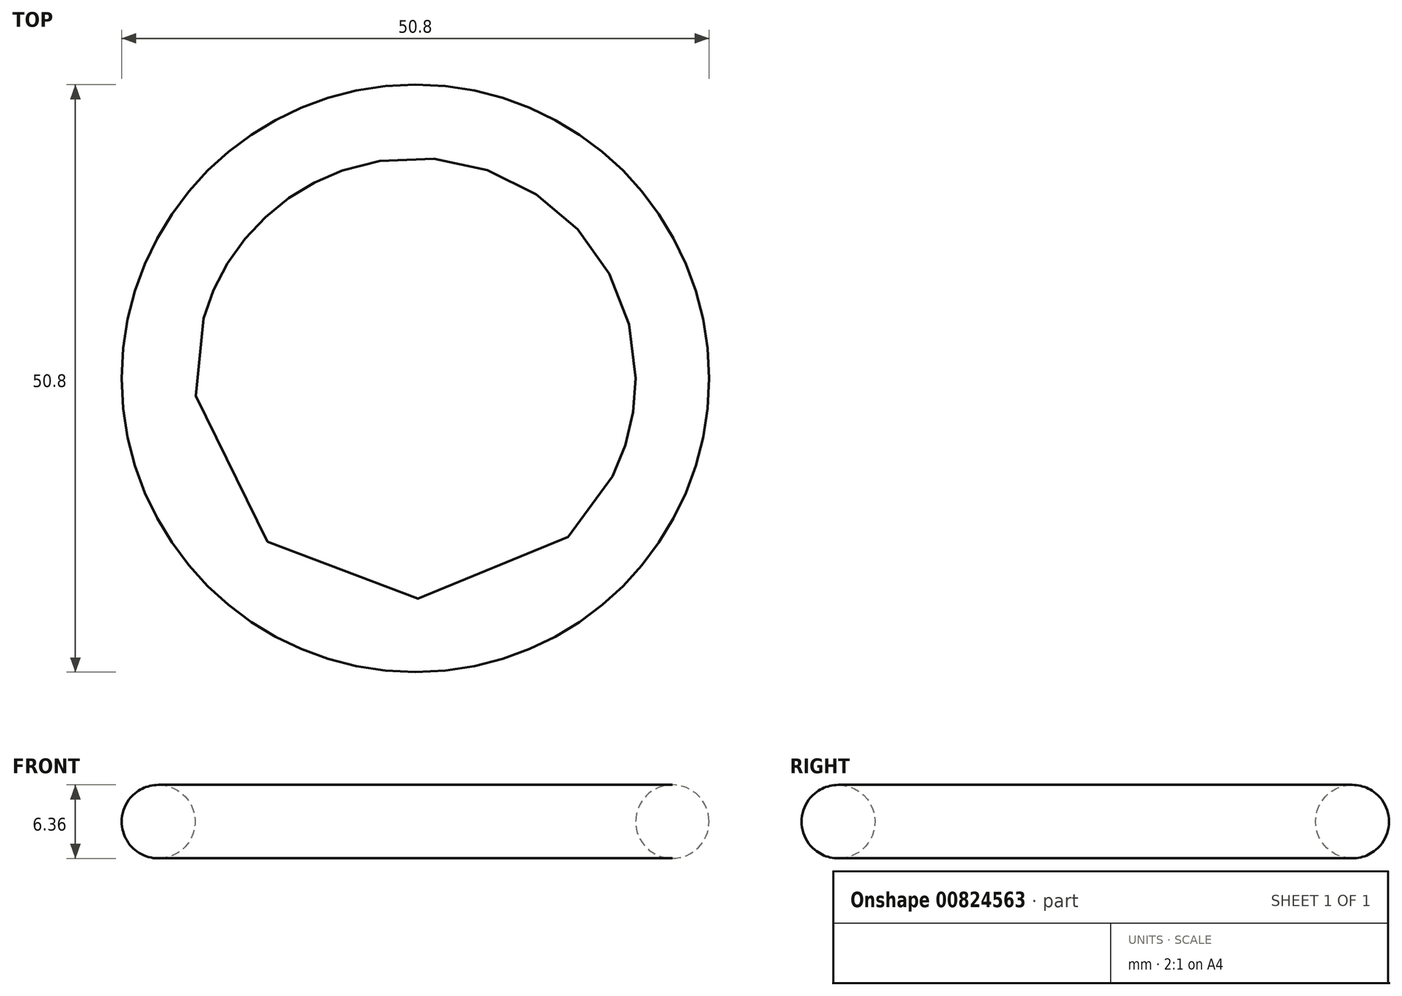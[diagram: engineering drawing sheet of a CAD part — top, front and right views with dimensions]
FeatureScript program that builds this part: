
annotation { "Feature Type Name" : "Feature", "Feature Type Description" : "" }
export const myFeature = defineFeature(function(context is Context, id is Id, definition is map)
    precondition{}
    {
        {
            var Q0;
            Q0=qCreatedBy(makeId("Front.planeOp"),FACE);
            var sketch = newSketch(context, id + "F0", { "sketchPlane" : qUnion([Q0])});
            skCircle(sketch, "E0", {"center": v(-22.23, 0) * mm, "radius": 3.18 * mm});
            skLineSegment(sketch, "E1", {"start": v(0, 12.94) * mm, "end": v(0, -10.9) * mm, "construction": true});
            skSolve(sketch);
        }
        {
            var Q0;
            Q0 = qSketchRegion(id + "F0", true);
            var Q1;
            Q1=sQuery(id+"F0.wireOp",EDGE,"E1");
            revolve(context, id + "F1", {"surfaceOperationType" : NewSurfaceOperationType.NEW, "entities" : qUnion([Q0]), "axis" : qUnion([Q1]), "revolveType" : RevolveType.FULL});
        }
    });
